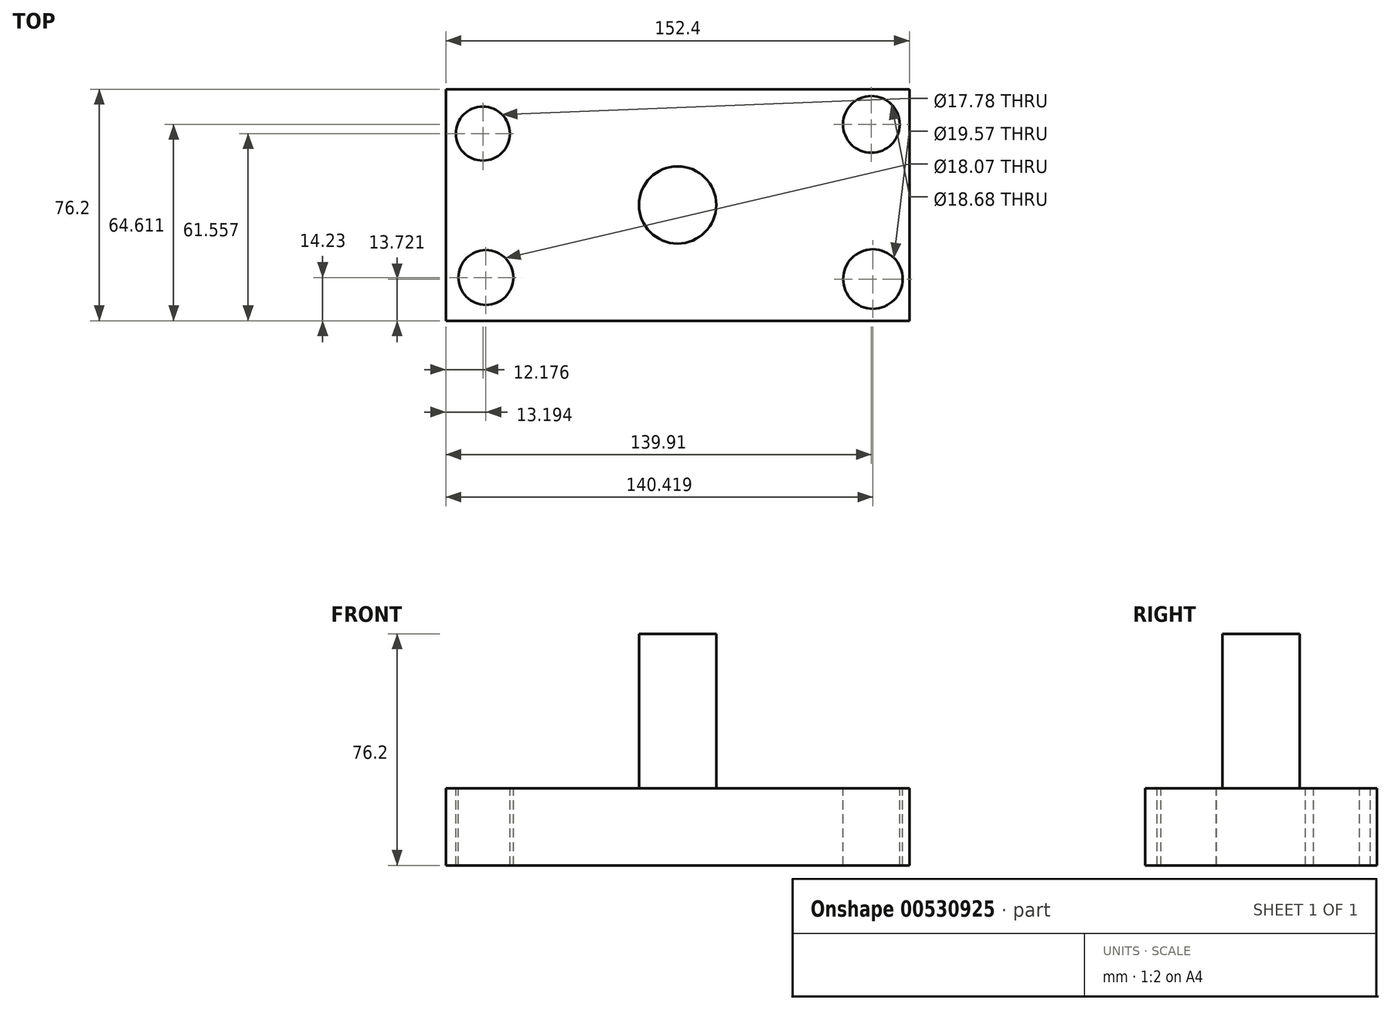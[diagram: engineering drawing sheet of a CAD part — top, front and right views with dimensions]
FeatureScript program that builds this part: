
annotation { "Feature Type Name" : "Feature", "Feature Type Description" : "" }
export const myFeature = defineFeature(function(context is Context, id is Id, definition is map)
    precondition{}
    {
        {
            var Q0;
            Q0=qCreatedBy(makeId("Top.planeOp"),FACE);
            var sketch = newSketch(context, id + "F0", { "sketchPlane" : qUnion([Q0])});
            skLineSegment(sketch, "E0.bottom", {"start": v(76.2, 38.1) * mm, "end": v(-76.2, 38.1) * mm});
            skLineSegment(sketch, "E0.top", {"start": v(76.2, -38.1) * mm, "end": v(-76.2, -38.1) * mm});
            skLineSegment(sketch, "E0.left", {"start": v(76.2, 38.1) * mm, "end": v(76.2, -38.1) * mm});
            skLineSegment(sketch, "E0.right", {"start": v(-76.2, 38.1) * mm, "end": v(-76.2, -38.1) * mm});
            skPoint(sketch, "E0.middle", {"position": v(0, 0) * mm});
            skSolve(sketch);
        }
        {
            var Q0;
            Q0=makeQuery(id+"F0.imprint","IMPRINT",FACE,{"disambiguationData":[TD([[makeQuery(id+"F0.imprint","IMPRINT",EDGE,{"derivedFrom":sQuery(id+"F0.wireOp",EDGE,"E0.bottom")}),1.0]])]});
            extrude(context, id + "F1", {"entities" : qUnion([Q0]), "oppositeDirection" : true, "depth" : 25.4 * mm, "offsetDistance" : 25.4 * mm});
        }
        {
            var Q0;
            Q0=qCreatedBy(makeId("Top.planeOp"),FACE);
            var sketch = newSketch(context, id + "F2", { "sketchPlane" : qUnion([Q0])});
            skCircle(sketch, "E1", {"center": v(64.22, -24.38) * mm, "radius": 9.79 * mm});
            skCircle(sketch, "E2", {"center": v(-63, -23.87) * mm, "radius": 9.03 * mm});
            skCircle(sketch, "E3", {"center": v(63.71, 26.51) * mm, "radius": 9.34 * mm});
            skCircle(sketch, "E4", {"center": v(-64.02, 23.46) * mm, "radius": 8.9 * mm});
            skSolve(sketch);
        }
        {
            var Q0;
            Q0=makeQuery(id+"F2.imprint","IMPRINT",FACE,{"disambiguationData":[TD([[makeQuery(id+"F2.imprint","IMPRINT",EDGE,{"derivedFrom":sQuery(id+"F2.wireOp",EDGE,"E4")}),1.0]])]});
            var Q1;
            Q1=makeQuery(id+"F2.imprint","IMPRINT",FACE,{"disambiguationData":[TD([[makeQuery(id+"F2.imprint","IMPRINT",EDGE,{"derivedFrom":sQuery(id+"F2.wireOp",EDGE,"E3")}),1.0]])]});
            var Q2;
            Q2=makeQuery(id+"F2.imprint","IMPRINT",FACE,{"disambiguationData":[TD([[makeQuery(id+"F2.imprint","IMPRINT",EDGE,{"derivedFrom":sQuery(id+"F2.wireOp",EDGE,"E2")}),1.0]])]});
            var Q3;
            Q3=makeQuery(id+"F2.imprint","IMPRINT",FACE,{"disambiguationData":[TD([[makeQuery(id+"F2.imprint","IMPRINT",EDGE,{"derivedFrom":sQuery(id+"F2.wireOp",EDGE,"E1")}),1.0]])]});
            var Q4;
            Q4=sQuery(id+"F2.wireOp",EDGE,"E4");
            extrude(context, id + "F3", {"entities" : qUnion([Q0, Q1, Q2, Q3]), "operationType" : NewBodyOperationType.REMOVE, "surfaceEntities" : qUnion([Q4]), "oppositeDirection" : true, "depth" : 50.8 * mm, "offsetDistance" : 25.4 * mm});
        }
        {
            var Q0;
            Q0=qCreatedBy(makeId("Front.planeOp"),FACE);
            var sketch = newSketch(context, id + "F4", { "sketchPlane" : qUnion([Q0])});
            skLineSegment(sketch, "E5.bottom", {"start": v(0, 0) * mm, "end": v(12.7, 0) * mm});
            skLineSegment(sketch, "E5.top", {"start": v(0, 50.8) * mm, "end": v(12.7, 50.8) * mm});
            skLineSegment(sketch, "E5.left", {"start": v(0, 0) * mm, "end": v(0, 50.8) * mm});
            skLineSegment(sketch, "E5.right", {"start": v(12.7, 0) * mm, "end": v(12.7, 50.8) * mm});
            skSolve(sketch);
        }
        {
            var Q0;
            Q0=makeQuery(id+"F4.imprint","IMPRINT",FACE,{"disambiguationData":[TD([[makeQuery(id+"F4.imprint","IMPRINT",EDGE,{"derivedFrom":sQuery(id+"F4.wireOp",EDGE,"E5.bottom")}),1.0]])]});
            var Q1;
            Q1=sQuery(id+"F4.wireOp",EDGE,"E5.left");
            revolve(context, id + "F5", {"operationType" : NewBodyOperationType.ADD, "entities" : qUnion([Q0]), "axis" : qUnion([Q1]), "revolveType" : RevolveType.FULL});
        }
    });
